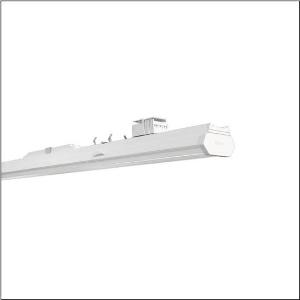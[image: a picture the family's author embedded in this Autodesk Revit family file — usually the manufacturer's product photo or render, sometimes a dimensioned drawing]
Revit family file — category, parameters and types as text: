
# Revit family: licross_r__11_protected_ho_51td11dn4f5s_b27d
name_source: partatom
category: Lighting Fixtures
units: mm (PartAtom-declared; Revit-internal decimal feet)

## family parameters
Cut with Voids When Loaded = No
Host = Face
Light Source = No
Part Type = Normal
Room Calculation Point = No
Round Connector Dimension = Use Diameter
Shared = No

## types (1)
- --- (1 x LED, 15510 lm, 87.3 W, 4000K)
    Apparent Load = 87 VA
    CIE Flux Codes = 84 94 98 99 100
    Color Rendering = 80
    Color Temperature = 4000K
    Default Elevation = 1800 mm
    Description = Licross® 11 Protected HO, luminaire insert, of sheet steel, galvanised, coil coated, white, length: 1.500mm, width: 90mm, height: 101mm, LED rated luminous flux: 15.510lm, light colour: 840, control gear: DALI 2, with plug, 5-pole, with phase selection, mains connection: 220..240V, AC, 50/60Hz, rated input power: 87W, halogen-free wiring, primary light control with lens, of plastic, primary optical cover: cover, of PMMA, light emission: direct distribution, primary light characteristic: symmetric, protection rating (complete): IP54, insulation class (complete): insulation class I (protective earthing), certification: CE, ENEC, VDE, UKCA, protection symbol: D if used in an environment with non-conductive dust loads with corresponding accessories, impact resistance: IK06, permissible ambient temperature for indoor applications: -25..+30°C, corresponds to IFS (International Featured Standards) requirements for safety and quality in the food industry, reducing of maximum allowable ambient temperature of 5°C with ceiling mounting, LABS conformity tested according to VDMA 24364:2018-05, packaging unit: 1 piece
    Height = 92 mm
    Lamp = 1 x LED
    Lamp Light Flux = 15510 lm
    Lamp Power = 87.3 W
    Lamp count = 1
    Length = 1500 mm
    Luminous efficacy = 178 lm/W
    Manufacturer = Siteco
    ModVariant = No
    Model = 51TD11DN4F5S
    Mounting Place = Ceiling
    Mounting Type = Pendant
    Number of Poles = 1
    OnlyDefault = Yes
    Power Factor = 1
    Product Name = Licross® 11 Protected HO
    Product group = luminaire insert
    ProductGroupID = 901
    Protection Class = Protection class I
    Protection Degree = IP 54
    RLX_Detail_Level = 1
    RLX_Emergency_Light_Flux = 0 lm
    RLX_Emergency_Type = 0
    RLX_Emergency_Type_DB = No
    RlxData = <blob elided: 24361 chars, md5=5a0b13af>
    Socket = socket
    Standby Power = 0 W
    System Light Flux = 15510 lm
    System Power = 87 W
    Type Comments = factory setting: luminous flux: 100 % | dim-lin: 254 | 589 mA
    Type Image = l_1256145.jpg
    URL = http://relux.com
    VarID = @adj_069945
    Voltage = 0 V
    Weight = 0.00 kg
    Width = 88 mm

## geometry (parser evidence)
native form markers: Blend x4, Sweep x11
no freeform markers — native parametric forms only
